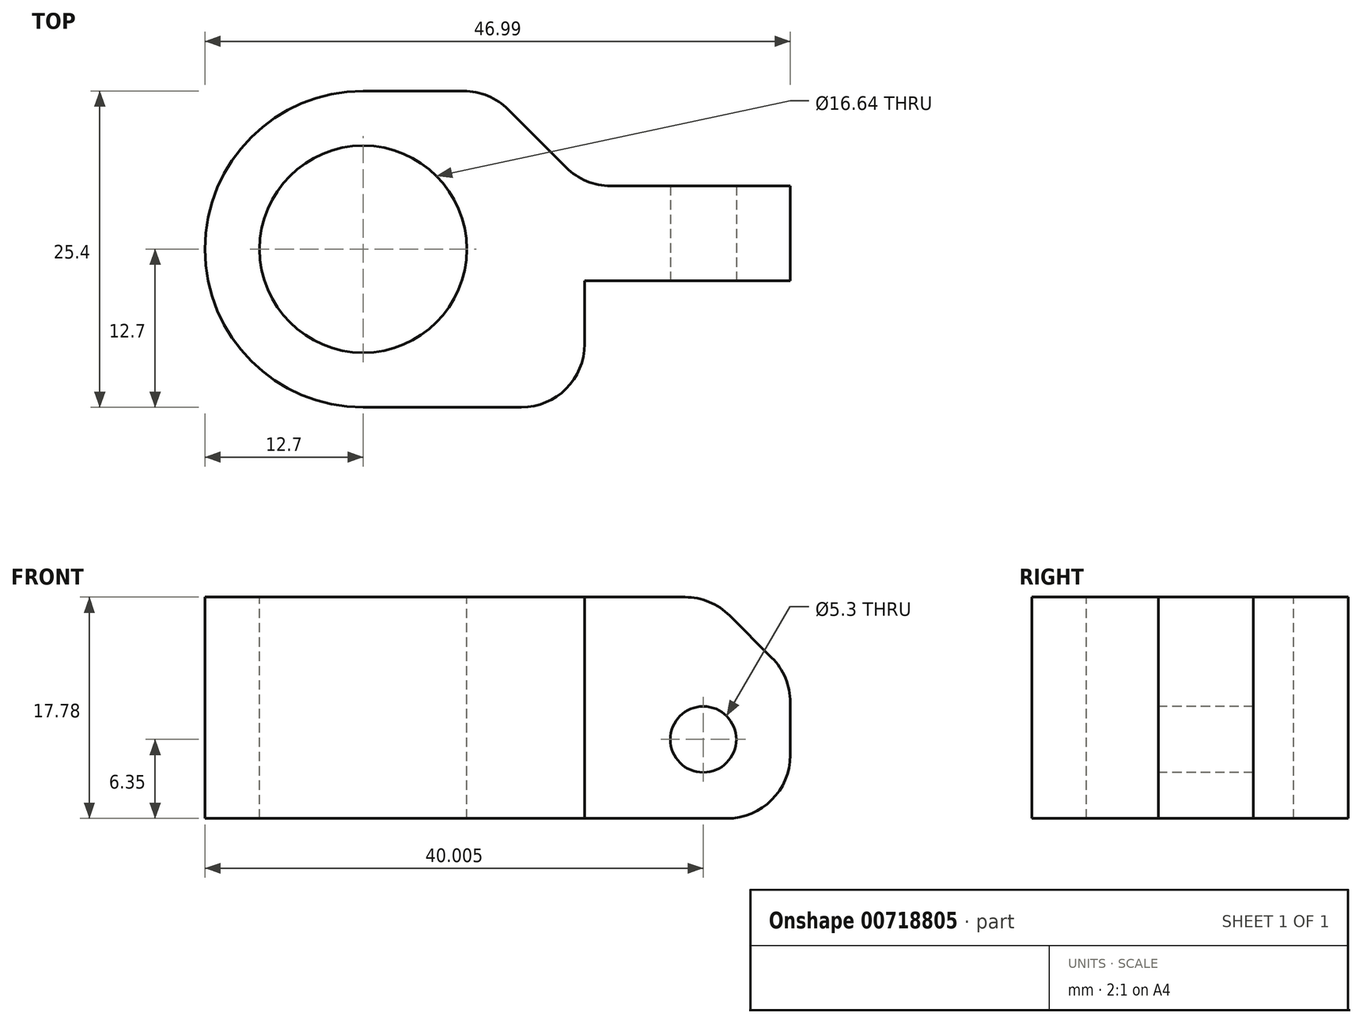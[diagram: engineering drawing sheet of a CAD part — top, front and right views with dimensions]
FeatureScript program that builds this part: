
annotation { "Feature Type Name" : "Feature", "Feature Type Description" : "" }
export const myFeature = defineFeature(function(context is Context, id is Id, definition is map)
    precondition{}
    {
        {
            var Q0;
            Q0=qCreatedBy(makeId("Top.planeOp"),FACE);
            var sketch = newSketch(context, id + "F0", { "sketchPlane" : qUnion([Q0])});
            skLineSegment(sketch, "E0", {"start": v(0, -12.7) * mm, "end": v(17.78, -12.7) * mm});
            skLineSegment(sketch, "E1", {"start": v(10.16, 12.7) * mm, "end": v(17.78, 5.08) * mm});
            skPoint(sketch, "E2.endSnap0", {"position": v(17.78, -12.7) * mm});
            skLineSegment(sketch, "E3", {"start": v(17.78, 5.08) * mm, "end": v(17.78, -12.7) * mm});
            skPoint(sketch, "E4.orphan", {"position": v(35.56, -12.7) * mm});
            skLineSegment(sketch, "E5", {"start": v(0, 12.7) * mm, "end": v(0, -12.7) * mm});
            skPoint(sketch, "E6", {"position": v(0, 0) * mm});
            skLineSegment(sketch, "E7", {"start": v(0, 12.7) * mm, "end": v(10.16, 12.7) * mm});
            skSolve(sketch);
        }
        {
            var Q0;
            Q0=makeQuery(id+"F0.imprint","IMPRINT",FACE,{"disambiguationData":[TD([[makeQuery(id+"F0.imprint","IMPRINT",EDGE,{"derivedFrom":sQuery(id+"F0.wireOp",EDGE,"ketpRVbD-6SFL-thPw-nqCE-cJDCLMVs4f7w")}),-1.0]])]});
            var Q1;
            Q1=makeQuery(id+"F0.imprint","IMPRINT",FACE,{"disambiguationData":[TD([[makeQuery(id+"F0.imprint","IMPRINT",EDGE,{"derivedFrom":sQuery(id+"F0.wireOp",EDGE,"kwQTg01m-MB6S-0rhp-ZYhS-7lbITb5VAH2c")}),1.0]])]});
            var Q2;
            Q2=makeQuery(id+"F0.imprint","IMPRINT",FACE,{"disambiguationData":[TD([[makeQuery(id+"F0.imprint","IMPRINT",EDGE,{"derivedFrom":sQuery(id+"F0.wireOp",EDGE,"E0")}),1.0]])]});
            extrude(context, id + "F1", {"entities" : qUnion([Q0, Q1, Q2]), "depth" : 17.78 * mm, "offsetDistance" : 25.4 * mm});
        }
        {
            var Q0;
            Q0=makeQuery(id+"F1.opExtrude","SWEPT_FACE",FACE,{"disambiguationData":[OSD([sQuery(id+"F0.wireOp",EDGE,"E3")])]});
            var sketch = newSketch(context, id + "F2", { "sketchPlane" : qUnion([Q0])});
            skLineSegment(sketch, "E8", {"start": v(5.08, 0) * mm, "end": v(5.08, 17.78) * mm});
            skLineSegment(sketch, "E9", {"start": v(5.08, 17.78) * mm, "end": v(-2.54, 17.78) * mm});
            skLineSegment(sketch, "E10", {"start": v(-2.54, 17.78) * mm, "end": v(-2.54, 0) * mm});
            skLineSegment(sketch, "E11", {"start": v(-2.54, 0) * mm, "end": v(5.08, 0) * mm});
            skSolve(sketch);
        }
        {
            var Q0;
            Q0=qSketchRegion(id+"F2",true);
            extrude(context, id + "F3", {"entities" : qUnion([Q0]), "operationType" : NewBodyOperationType.ADD, "depth" : 16.5 * mm, "offsetDistance" : 25.4 * mm});
        }
        {
            var Q0;
            Q0=makeQuery(id+"F3.opExtrude","CAP_EDGE",EDGE,{"disambiguationData":[OSD([sQuery(id+"F2.wireOp",EDGE,"iHOXsHoF-hqfp-rUCR-3NdC-NWc7uM61uAc2")])],"isStart":false});
            var Q1;
            Q1=makeQuery(id+"F3.opExtrude","CAP_EDGE",EDGE,{"disambiguationData":[OSD([sQuery(id+"F2.wireOp",EDGE,"E9")])],"isStart":false});
            chamfer(context, id + "F4", {"entities" : qUnion([Q0, Q1]), "width" : 6.35 * mm, "tangentPropagation" : true});
        }
        {
            var Q0;
            Q0=makeQuery(id+"F3.opExtrude","SWEPT_FACE",FACE,{"disambiguationData":[OSD([sQuery(id+"F2.wireOp",EDGE,"E10")])]});
            var sketch = newSketch(context, id + "F5", { "sketchPlane" : qUnion([Q0])});
            skCircle(sketch, "E12", {"center": v(27.3, 6.35) * mm, "radius": 2.65 * mm});
            skSolve(sketch);
        }
        {
            var Q0;
            Q0=qSketchRegion(id+"F5",true);
            extrude(context, id + "F6", {"entities" : qUnion([Q0]), "operationType" : NewBodyOperationType.REMOVE, "oppositeDirection" : true, "depth" : 25.4 * mm, "offsetDistance" : 25.4 * mm});
        }
        {
            var Q0;
            Q0=makeQuery(id+"F1.opExtrude","SWEPT_EDGE",EDGE,{"disambiguationData":[OSD([sQuery(id+"F0.wireOp",EDGE,"lA7RWFjU-o6z8-oVj1-BCSd-RaWdqnYN69Uw"),sQuery(id+"F0.wireOp",EDGE,"E1")])]});
            fillet(context, id + "F7", {"entities" : qUnion([Q0]), "radius" : 5.08 * mm, "tangentPropagation" : true, "allowEdgeOverflow" : false});
        }
        {
            var Q0;
            Q0=makeQuery(id+"F3.opExtrude","CAP_EDGE",EDGE,{"disambiguationData":[OSD([sQuery(id+"F2.wireOp",EDGE,"E11")])],"isStart":false});
            fillet(context, id + "F8", {"entities" : qUnion([Q0]), "radius" : 5.08 * mm, "tangentPropagation" : true, "allowEdgeOverflow" : false});
        }
        {
            var Q0;
            Q0=makeQuery(id+"F1.opExtrude","SWEPT_EDGE",EDGE,{"disambiguationData":[OSD([sQuery(id+"F0.wireOp",EDGE,"E0"),sQuery(id+"F0.wireOp",EDGE,"E3")])]});
            fillet(context, id + "F9", {"entities" : qUnion([Q0]), "radius" : 5.08 * mm, "tangentPropagation" : true, "allowEdgeOverflow" : false});
        }
        {
            var Q0;
            {var subQ0=sQuery(id+"F2.wireOp",EDGE,"E9");Q0=makeQuery(id+"F4.opChamfer","BLEND_EDGE",EDGE,{"blendedFrom":[makeQuery(id+"F3.opExtrude","CAP_EDGE",EDGE,{"disambiguationData":[OSD([subQ0])],"isStart":false}),makeQuery(id+"F3.opExtrude","CAP_FACE",FACE,{"disambiguationData":[OSD([sQuery(id+"F2.wireOp",EDGE,"E8"),subQ0,sQuery(id+"F2.wireOp",EDGE,"E10"),sQuery(id+"F2.wireOp",EDGE,"E11")])],"isStart":false})],"blendedInto":[makeQuery(id+"F3.opExtrude","CAP_FACE",FACE,{"disambiguationData":[OSD([sQuery(id+"F2.wireOp",EDGE,"E8"),subQ0,sQuery(id+"F2.wireOp",EDGE,"E10"),sQuery(id+"F2.wireOp",EDGE,"E11")])],"isStart":false})]});}
            var Q1;
            {var subQ0=sQuery(id+"F2.wireOp",EDGE,"E9");Q1=makeQuery(id+"F4.opChamfer","BLEND_EDGE",EDGE,{"blendedFrom":[makeQuery(id+"F3.opExtrude","CAP_EDGE",EDGE,{"disambiguationData":[OSD([subQ0])],"isStart":false}),makeQuery(id+"F3.boolean.opBoolean","MERGE",FACE,{"derivedFrom":[makeQuery(id+"F1.opExtrude","CAP_FACE",FACE,{"disambiguationData":[OSD([sQuery(id+"F0.wireOp",EDGE,"kwQTg01m-MB6S-0rhp-ZYhS-7lbITb5VAH2c"),sQuery(id+"F0.wireOp",EDGE,"ZW4eHoN5-aVj7-xQgZ-3iqp-MtelBjjwJpwb"),sQuery(id+"F0.wireOp",EDGE,"CEKv87Bx-M4Om-Dnog-52Co-38QzP6SqRSkZ"),sQuery(id+"F0.wireOp",EDGE,"L3x0mkI3-XsUk-m9FF-a0Xz-Nz5ZdZdmJitv"),sQuery(id+"F0.wireOp",EDGE,"E0"),sQuery(id+"F0.wireOp",EDGE,"lA7RWFjU-o6z8-oVj1-BCSd-RaWdqnYN69Uw"),sQuery(id+"F0.wireOp",EDGE,"E1"),sQuery(id+"F0.wireOp",EDGE,"E3"),sQuery(id+"F0.wireOp",EDGE,"Q6sN5krz-uvas-wkKX-Y54k-tdkdmb1LrcdW"),sQuery(id+"F0.wireOp",EDGE,"ZyEIM47p-abHS-fnEs-x0dx-Lz7iyDPNLUu2"),sQuery(id+"F0.wireOp",EDGE,"FxLzZaPg-Jl4A-2pC9-M360-u8lN6izDk8dW"),sQuery(id+"F0.wireOp",EDGE,"ABsG3OGm-gQbB-QsGX-5SIj-NiBecTxfoq32"),sQuery(id+"F0.wireOp",EDGE,"kIHzTZGS-4pHM-WRKg-CVcm-TUqsQQeTlhpI"),sQuery(id+"F0.wireOp",EDGE,"GMHOo6fi-2uvi-hdSo-vLzN-bD14R9f7cwBq")])],"isStart":false}),makeQuery(id+"F3.opExtrude","SWEPT_FACE",FACE,{"disambiguationData":[OSD([subQ0])]})]})],"blendedInto":[makeQuery(id+"F3.boolean.opBoolean","MERGE",FACE,{"derivedFrom":[makeQuery(id+"F1.opExtrude","CAP_FACE",FACE,{"disambiguationData":[OSD([sQuery(id+"F0.wireOp",EDGE,"kwQTg01m-MB6S-0rhp-ZYhS-7lbITb5VAH2c"),sQuery(id+"F0.wireOp",EDGE,"ZW4eHoN5-aVj7-xQgZ-3iqp-MtelBjjwJpwb"),sQuery(id+"F0.wireOp",EDGE,"CEKv87Bx-M4Om-Dnog-52Co-38QzP6SqRSkZ"),sQuery(id+"F0.wireOp",EDGE,"L3x0mkI3-XsUk-m9FF-a0Xz-Nz5ZdZdmJitv"),sQuery(id+"F0.wireOp",EDGE,"E0"),sQuery(id+"F0.wireOp",EDGE,"lA7RWFjU-o6z8-oVj1-BCSd-RaWdqnYN69Uw"),sQuery(id+"F0.wireOp",EDGE,"E1"),sQuery(id+"F0.wireOp",EDGE,"E3"),sQuery(id+"F0.wireOp",EDGE,"Q6sN5krz-uvas-wkKX-Y54k-tdkdmb1LrcdW"),sQuery(id+"F0.wireOp",EDGE,"ZyEIM47p-abHS-fnEs-x0dx-Lz7iyDPNLUu2"),sQuery(id+"F0.wireOp",EDGE,"FxLzZaPg-Jl4A-2pC9-M360-u8lN6izDk8dW"),sQuery(id+"F0.wireOp",EDGE,"ABsG3OGm-gQbB-QsGX-5SIj-NiBecTxfoq32"),sQuery(id+"F0.wireOp",EDGE,"kIHzTZGS-4pHM-WRKg-CVcm-TUqsQQeTlhpI"),sQuery(id+"F0.wireOp",EDGE,"GMHOo6fi-2uvi-hdSo-vLzN-bD14R9f7cwBq")])],"isStart":false}),makeQuery(id+"F3.opExtrude","SWEPT_FACE",FACE,{"disambiguationData":[OSD([subQ0])]})]})]});}
            fillet(context, id + "F10", {"entities" : qUnion([Q0, Q1]), "radius" : 5.08 * mm, "tangentPropagation" : true, "allowEdgeOverflow" : false});
        }
        {
            var Q0;
            Q0=makeQuery(id+"F3.boolean.opBoolean","MERGE",FACE,{"derivedFrom":[makeQuery(id+"F1.opExtrude","CAP_FACE",FACE,{"disambiguationData":[OSD([sQuery(id+"F0.wireOp",EDGE,"E0"),sQuery(id+"F0.wireOp",EDGE,"lA7RWFjU-o6z8-oVj1-BCSd-RaWdqnYN69Uw"),sQuery(id+"F0.wireOp",EDGE,"E1"),sQuery(id+"F0.wireOp",EDGE,"E3"),sQuery(id+"F0.wireOp",EDGE,"kIHzTZGS-4pHM-WRKg-CVcm-TUqsQQeTlhpI"),sQuery(id+"F0.wireOp",EDGE,"E5")])],"isStart":false}),makeQuery(id+"F3.opExtrude","SWEPT_FACE",FACE,{"disambiguationData":[OSD([sQuery(id+"F2.wireOp",EDGE,"E9")])]})]});
            var sketch = newSketch(context, id + "F11", { "sketchPlane" : qUnion([Q0])});
            skPoint(sketch, "E13.center.orphan", {"position": v(0, 0) * mm});
            skLineSegment(sketch, "E14", {"start": v(0, -12.7) * mm, "end": v(0, -12.7) * mm});
            skArc(sketch, "E15", {"start": v(0, 12.7) * mm, "mid": v(-12.7, 0) * mm, "end": v(0, -12.7) * mm});
            skLineSegment(sketch, "E16.0", {"start": v(0, 12.7) * mm, "end": v(0, -12.7) * mm});
            skSolve(sketch);
        }
        {
            var Q0;
            Q0=makeQuery(id+"F11.imprint","IMPRINT",FACE,{"disambiguationData":[TD([[makeQuery(id+"F11.imprint","IMPRINT",EDGE,{"derivedFrom":sQuery(id+"F11.wireOp",EDGE,"E14")}),1.0]])]});
            var Q1;
            Q1=makeQuery(id+"F11.imprint","IMPRINT",FACE,{"disambiguationData":[TD([[makeQuery(id+"F11.imprint","IMPRINT",EDGE,{"derivedFrom":sQuery(id+"F11.wireOp",EDGE,"E15")}),1.0]])]});
            var Q2;
            Q2=makeQuery(id+"F3.boolean.opBoolean","MERGE",FACE,{"derivedFrom":[makeQuery(id+"F1.opExtrude","CAP_FACE",FACE,{"disambiguationData":[OSD([sQuery(id+"F0.wireOp",EDGE,"E0"),sQuery(id+"F0.wireOp",EDGE,"lA7RWFjU-o6z8-oVj1-BCSd-RaWdqnYN69Uw"),sQuery(id+"F0.wireOp",EDGE,"E1"),sQuery(id+"F0.wireOp",EDGE,"E3"),sQuery(id+"F0.wireOp",EDGE,"kIHzTZGS-4pHM-WRKg-CVcm-TUqsQQeTlhpI"),sQuery(id+"F0.wireOp",EDGE,"E5")])],"isStart":true}),makeQuery(id+"F3.opExtrude","SWEPT_FACE",FACE,{"disambiguationData":[OSD([sQuery(id+"F2.wireOp",EDGE,"E11")])]})]});
            extrude(context, id + "F12", {"entities" : qUnion([Q0, Q1]), "operationType" : NewBodyOperationType.ADD, "endBound" : BoundingType.UP_TO_SURFACE, "oppositeDirection" : true, "depth" : 25.4 * mm, "endBoundEntityFace" : qUnion([Q2]), "offsetDistance" : 25.4 * mm});
        }
        {
            var Q0;
            Q0=makeQuery(id+"F12.boolean.opBoolean","MERGE",FACE,{"derivedFrom":[makeQuery(id+"F3.boolean.opBoolean","MERGE",FACE,{"derivedFrom":[makeQuery(id+"F1.opExtrude","CAP_FACE",FACE,{"disambiguationData":[OSD([sQuery(id+"F0.wireOp",EDGE,"E0"),sQuery(id+"F0.wireOp",EDGE,"E1"),sQuery(id+"F0.wireOp",EDGE,"E3"),sQuery(id+"F0.wireOp",EDGE,"E5"),sQuery(id+"F0.wireOp",EDGE,"E7")])],"isStart":false}),makeQuery(id+"F3.opExtrude","SWEPT_FACE",FACE,{"disambiguationData":[OSD([sQuery(id+"F2.wireOp",EDGE,"E9")])]})]}),makeQuery(id+"F12.opExtrude","CAP_FACE",FACE,{"disambiguationData":[OSD([sQuery(id+"F11.wireOp",EDGE,"E15"),sQuery(id+"F11.wireOp",EDGE,"E16.0")])],"isStart":true})]});
            var sketch = newSketch(context, id + "F13", { "sketchPlane" : qUnion([Q0])});
            skCircle(sketch, "E17", {"center": v(0, 0) * mm, "radius": 8.32 * mm});
            skSolve(sketch);
        }
        {
            var Q0;
            Q0=makeQuery(id+"F13.imprint","IMPRINT",FACE,{"disambiguationData":[TD([[makeQuery(id+"F13.imprint","IMPRINT",EDGE,{"derivedFrom":sQuery(id+"F13.wireOp",EDGE,"E17")}),1.0]])]});
            extrude(context, id + "F14", {"entities" : qUnion([Q0]), "operationType" : NewBodyOperationType.REMOVE, "endBound" : BoundingType.THROUGH_ALL, "oppositeDirection" : true, "depth" : 25.4 * mm, "offsetDistance" : 25.4 * mm});
        }
    });
